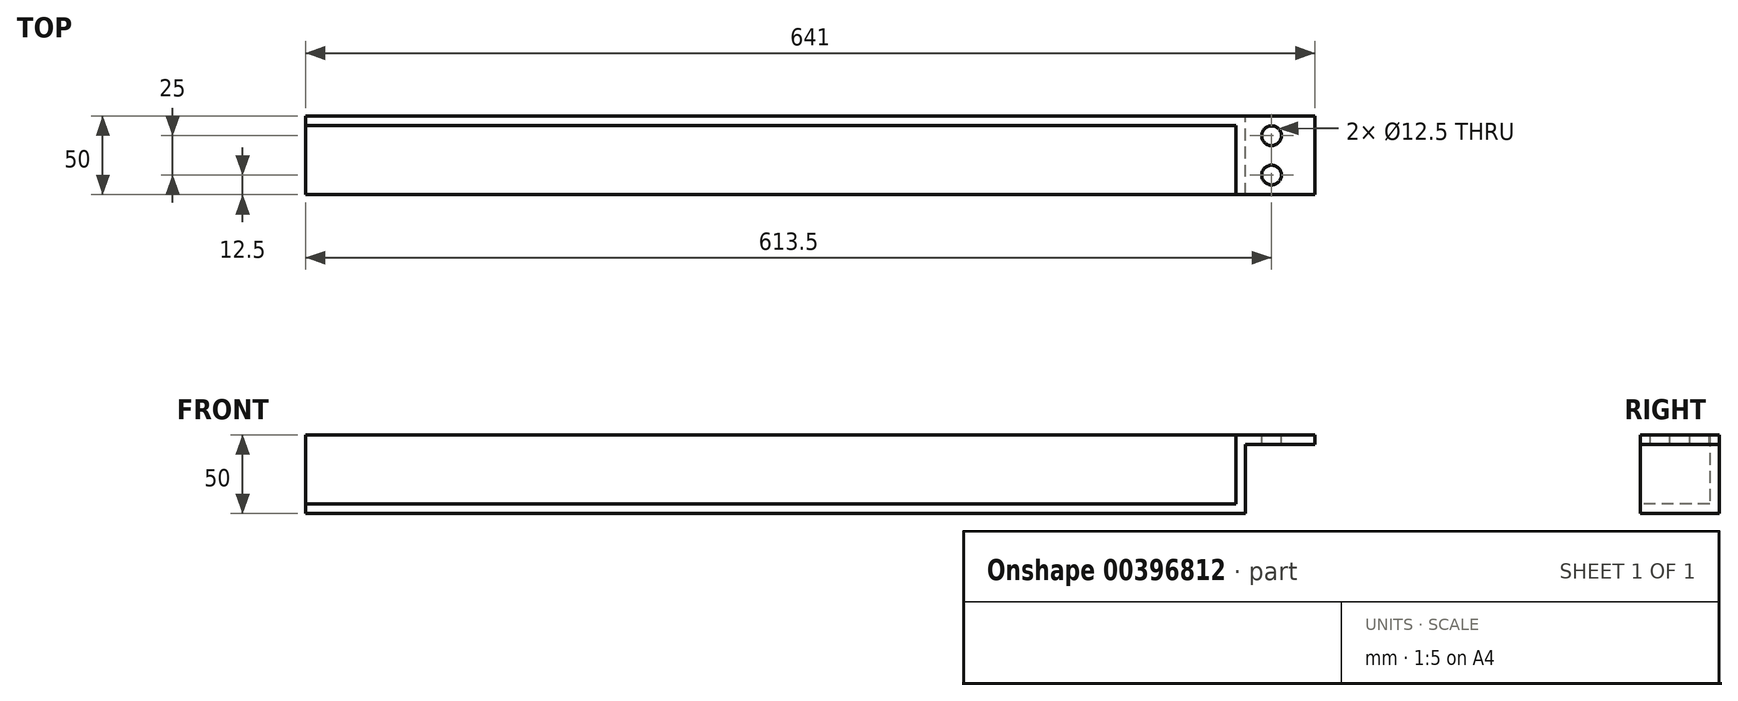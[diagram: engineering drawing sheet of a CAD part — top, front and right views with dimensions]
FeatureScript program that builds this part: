
annotation { "Feature Type Name" : "Feature", "Feature Type Description" : "" }
export const myFeature = defineFeature(function(context is Context, id is Id, definition is map)
    precondition{}
    {
        {
            var Q0;
            Q0=qCreatedBy(makeId("Right.planeOp"),FACE);
            var sketch = newSketch(context, id + "F0", { "sketchPlane" : qUnion([Q0])});
            skLineSegment(sketch, "E0", {"start": v(0, 0) * mm, "end": v(50, 0) * mm});
            skLineSegment(sketch, "E1", {"start": v(50, 0) * mm, "end": v(50, 50) * mm});
            skLineSegment(sketch, "E2", {"start": v(50, 50) * mm, "end": v(44, 50) * mm});
            skLineSegment(sketch, "E3", {"start": v(44, 50) * mm, "end": v(44, 6) * mm});
            skLineSegment(sketch, "E4", {"start": v(44, 6) * mm, "end": v(0, 6) * mm});
            skLineSegment(sketch, "E5", {"start": v(0, 6) * mm, "end": v(0, 0) * mm});
            skSolve(sketch);
        }
        {
            var Q0;
            Q0 = qSketchRegion(id + "F0", true);
            extrude(context, id + "F1", {"entities" : qUnion([Q0]), "endBound" : BoundingType.SYMMETRIC, "depth" : 591 * mm});
        }
        {
            var Q0;
            Q0=makeQuery(id+"F1.opExtrude","SWEPT_FACE",FACE,{"disambiguationData":[OSD([sQuery(id+"F0.wireOp",EDGE,"E1")])]});
            var sketch = newSketch(context, id + "F2", { "sketchPlane" : qUnion([Q0])});
            skLineSegment(sketch, "E6", {"start": v(-295.5, 0) * mm, "end": v(-301.5, 0) * mm});
            skLineSegment(sketch, "E7", {"start": v(-301.5, 0) * mm, "end": v(-301.5, 44) * mm});
            skLineSegment(sketch, "E8", {"start": v(-301.5, 44) * mm, "end": v(-345.5, 44) * mm});
            skLineSegment(sketch, "E9", {"start": v(-345.5, 44) * mm, "end": v(-345.5, 50) * mm});
            skLineSegment(sketch, "E10", {"start": v(-345.5, 50) * mm, "end": v(-295.5, 50) * mm});
            skSolve(sketch);
        }
        {
            var Q0;
            Q0=makeQuery(id+"F2.imprint","IMPRINT",FACE,{"disambiguationData":[TD([[makeQuery(id+"F2.imprint","IMPRINT",EDGE,{"derivedFrom":sQuery(id+"F2.wireOp",EDGE,"E6")}),-1.0]])]});
            extrude(context, id + "F3", {"entities" : qUnion([Q0]), "operationType" : NewBodyOperationType.ADD, "oppositeDirection" : true, "depth" : 50 * mm});
        }
        {
            var Q0;
            {var subQ0=sQuery(id+"F2.wireOp",EDGE,"E10");Q0=makeQuery(id+"Fr8UkPyPKDHse2f_1.1.F3.boolean.opBoolean","MERGE",FACE,{"derivedFrom":[makeQuery(id+"F3.boolean.opBoolean","MERGE",FACE,{"derivedFrom":[makeQuery(id+"F1.opExtrude","SWEPT_FACE",FACE,{"disambiguationData":[OSD([sQuery(id+"F0.wireOp",EDGE,"E2")])]}),makeQuery(id+"F3.opExtrude","SWEPT_FACE",FACE,{"disambiguationData":[OSD([subQ0])]})]}),makeQuery(id+"Fr8UkPyPKDHse2f_1.1.F3.opExtrude","SWEPT_FACE",FACE,{"disambiguationData":[OSD([subQ0])]})]});}
            var sketch = newSketch(context, id + "F4", { "sketchPlane" : qUnion([Q0])});
            skPoint(sketch, "E11", {"position": v(318, 37.5) * mm});
            skPoint(sketch, "E12", {"position": v(318, 12.5) * mm});
            skSolve(sketch);
        }
        {
            var Q0;
            Q0=sQuery(id+"F4.wireOp",VERTEX,"E11");
            var Q1;
            Q1=sQuery(id+"F4.wireOp",VERTEX,"E12");
            var Q2;
            Q2=makeQuery(id+"F1.opExtrude","SWEPT_BODY",BODY,{"disambiguationData":[OSD([sQuery(id+"F0.wireOp",EDGE,"E0"),sQuery(id+"F0.wireOp",EDGE,"E1"),sQuery(id+"F0.wireOp",EDGE,"E2"),sQuery(id+"F0.wireOp",EDGE,"E3"),sQuery(id+"F0.wireOp",EDGE,"E4"),sQuery(id+"F0.wireOp",EDGE,"E5")])]});
            hole(context, id + "F5", {"style" : HoleStyle.SIMPLE, "endStyle" : HoleEndStyle.THROUGH, "standardTappedOrClearance" : lookupTablePath({ "standard" : "ISO", "size" : "12.5", "type" : "Drilled" }), "standardBlindInLast" : lookupTablePath({ "standard" : "ISO", "size" : "12.5", "type" : "Drilled" }), "holeDiameter" : 12.5 * mm, "isTappedThrough" : true, "tappedDepth" : 12 * mm, "tapClearance" : 3, "locations" : qUnion([Q0, Q1]), "scope" : qUnion([Q2])});
        }
    });
